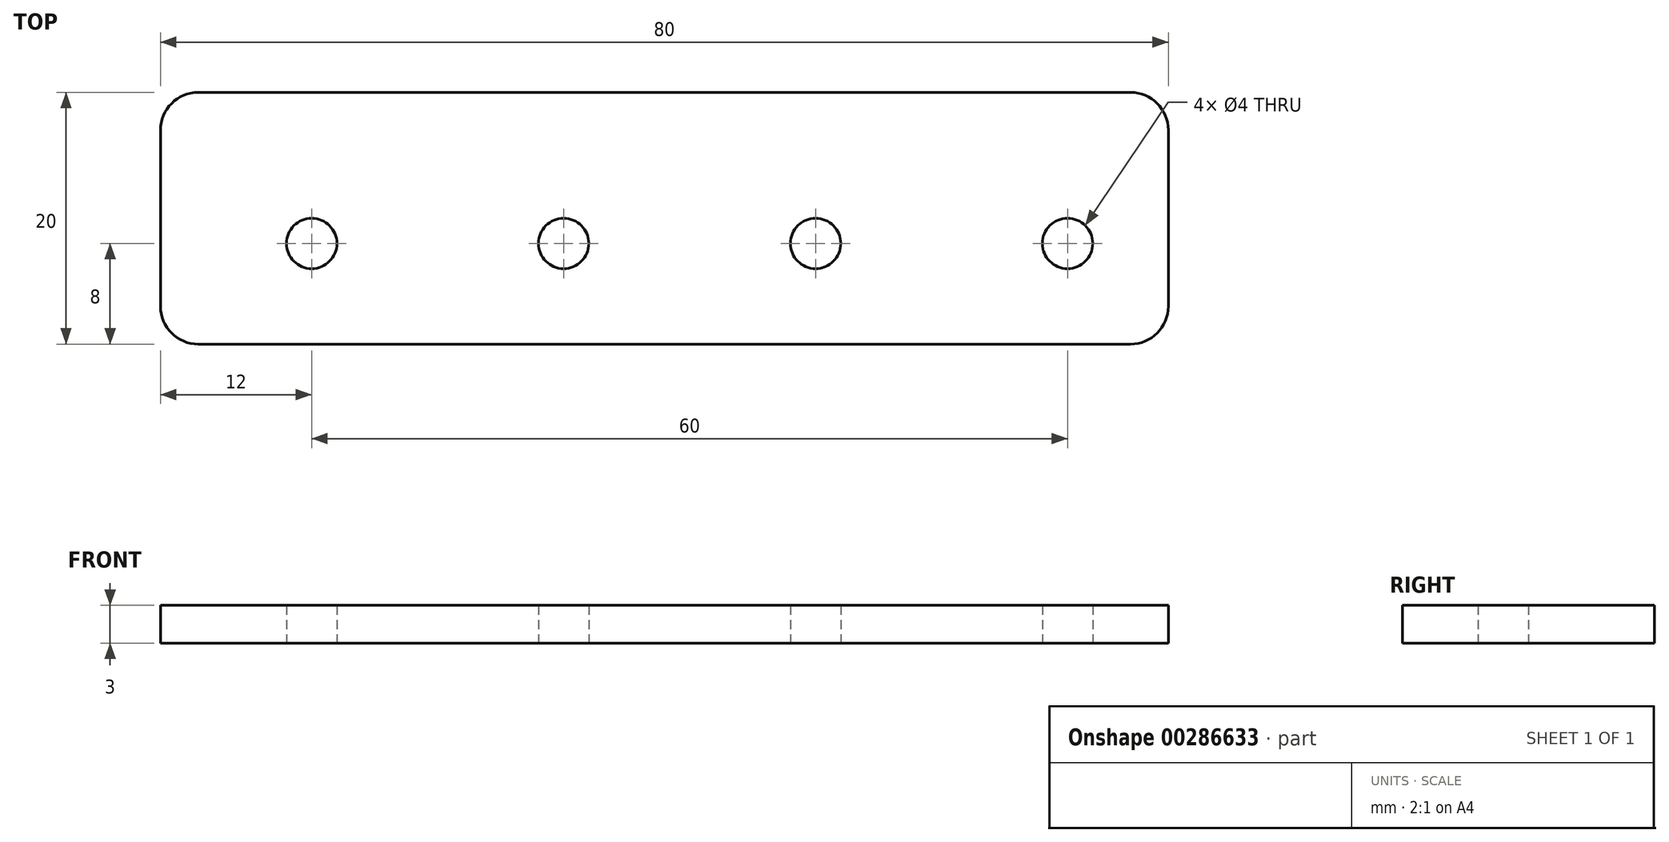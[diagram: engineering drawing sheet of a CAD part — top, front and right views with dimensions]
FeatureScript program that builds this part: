
annotation { "Feature Type Name" : "Feature", "Feature Type Description" : "" }
export const myFeature = defineFeature(function(context is Context, id is Id, definition is map)
    precondition{}
    {
        {
            var Q0;
            Q0=qCreatedBy(makeId("Top.planeOp"),FACE);
            var sketch = newSketch(context, id + "F0", { "sketchPlane" : qUnion([Q0])});
            skLineSegment(sketch, "E0.bottom", {"start": v(65, 12) * mm, "end": v(-9, 12) * mm});
            skLineSegment(sketch, "E0.top", {"start": v(65, -8) * mm, "end": v(-9, -8) * mm});
            skLineSegment(sketch, "E0.left", {"start": v(68, 9) * mm, "end": v(68, -5) * mm});
            skLineSegment(sketch, "E0.right", {"start": v(-12, 9) * mm, "end": v(-12, -5) * mm});
            skPoint(sketch, "E0.middle", {"position": v(0, 0) * mm});
            skCircle(sketch, "E1", {"center": v(0, 0) * mm, "radius": 2 * mm});
            skCircle(sketch, "E2.1.0.0", {"center": v(20, 0) * mm, "radius": 2 * mm});
            skCircle(sketch, "E2.2.0.0", {"center": v(40, 0) * mm, "radius": 2 * mm});
            skLineSegment(sketch, "E2.direction1", {"start": v(0, 0) * mm, "end": v(20, 0) * mm, "construction": true});
            skPoint(sketch, "E3.visualSharp", {"position": v(-12, 12) * mm});
            skArc(sketch, "E3.filletArc", {"start": v(-9, 12) * mm, "mid": v(-11.12, 11.12) * mm, "end": v(-12, 9) * mm});
            skPoint(sketch, "E4.visualSharp", {"position": v(68, 12) * mm});
            skArc(sketch, "E4.filletArc", {"start": v(68, 9) * mm, "mid": v(67.12, 11.12) * mm, "end": v(65, 12) * mm});
            skPoint(sketch, "E5.visualSharp", {"position": v(68, -8) * mm});
            skArc(sketch, "E5.filletArc", {"start": v(65, -8) * mm, "mid": v(67.12, -7.12) * mm, "end": v(68, -5) * mm});
            skPoint(sketch, "E6.visualSharp", {"position": v(-12, -8) * mm});
            skArc(sketch, "E6.filletArc", {"start": v(-12, -5) * mm, "mid": v(-11.12, -7.12) * mm, "end": v(-9, -8) * mm});
            skCircle(sketch, "E7.0.3.0", {"center": v(60, 0) * mm, "radius": 2 * mm});
            skSolve(sketch);
        }
        {
            var Q0;
            Q0 = qSketchRegion(id + "F0", true);
            extrude(context, id + "F1", {"entities" : qUnion([Q0]), "depth" : 3 * mm});
        }
    });
